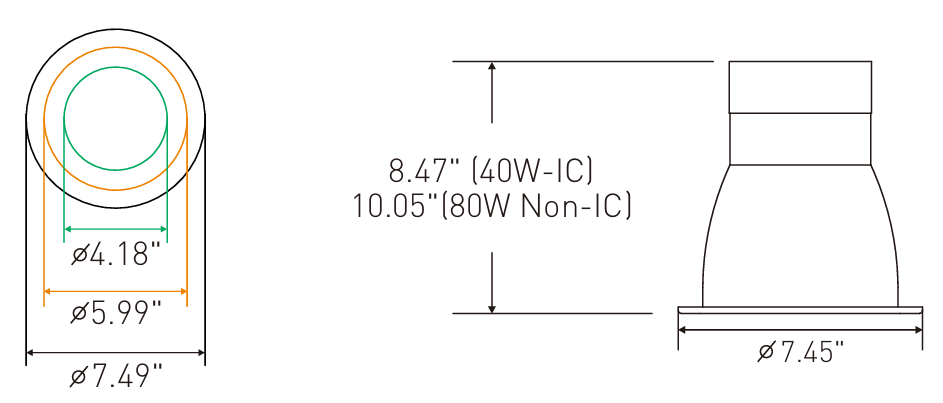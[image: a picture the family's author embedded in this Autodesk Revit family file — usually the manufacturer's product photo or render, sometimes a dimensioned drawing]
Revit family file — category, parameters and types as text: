
# Revit family: Alcon-14124-6-Revit-Family
name_source: partatom
category: Lighting Fixtures
units: mm (PartAtom-declared; Revit-internal decimal feet)

## family parameters
Always vertical = Yes
Cut with Voids When Loaded = No
Host = Ceiling
Light Source = Yes
OmniClass Number = 23.80.70.11
OmniClass Title = Luminaries for Internal Lighting
Part Type = Normal
Room Calculation Point = No
Round Connector Dimension = Use Diameter
Shared = No

## types (1)
- Type 1
    Color Filter = 16777215
    Default Elevation = 0' - 0"
    Dimming Lamp Color Temperature Shift = <None>
    Housing = <By Category>
    Lens = <By Category>
    Light Source Symbol Length = 10' - 0"
    LightSource = <By Category>
    Link To Product Page = https://www.alconlighting.com
    Manufacturer = Alcon Light
    Product Identity = Alcon Lighting 14124-6
    Spot Beam Angle = 30.00°
    Spot Field Angle = 90.00°
    Tilt Angle = 60.00°

## geometry (parser evidence)
native form markers: Sweep x3
no freeform markers — native parametric forms only
